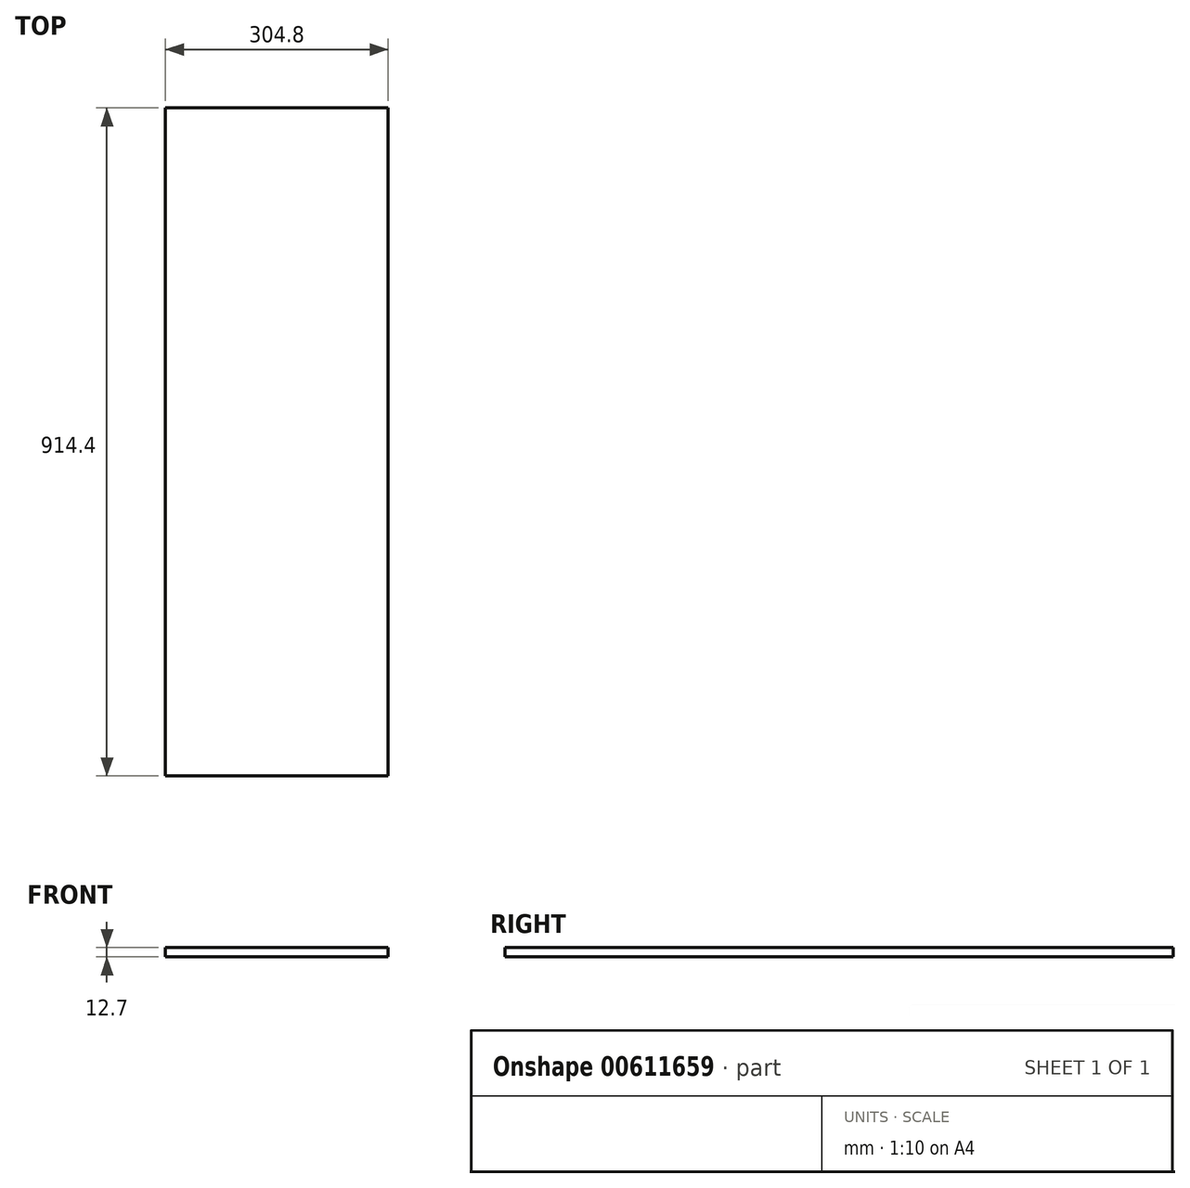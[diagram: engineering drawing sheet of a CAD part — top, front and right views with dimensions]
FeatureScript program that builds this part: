
annotation { "Feature Type Name" : "Feature", "Feature Type Description" : "" }
export const myFeature = defineFeature(function(context is Context, id is Id, definition is map)
    precondition{}
    {
        {
            var Q0;
            Q0=qCreatedBy(makeId("Top.planeOp"),FACE);
            var sketch = newSketch(context, id + "F0", { "sketchPlane" : qUnion([Q0])});
            skLineSegment(sketch, "E0.bottom", {"start": v(-152.4, 457.2) * mm, "end": v(152.4, 457.2) * mm});
            skLineSegment(sketch, "E0.top", {"start": v(-152.4, -457.2) * mm, "end": v(152.4, -457.2) * mm});
            skLineSegment(sketch, "E0.left", {"start": v(-152.4, 457.2) * mm, "end": v(-152.4, -457.2) * mm});
            skLineSegment(sketch, "E0.right", {"start": v(152.4, 457.2) * mm, "end": v(152.4, -457.2) * mm});
            skSolve(sketch);
        }
        {
            var Q0;
            Q0 = qSketchRegion(id + "FfFJr1QY6GmuVDC_0", true);
            var Q1;
            Q1=makeQuery(id+"F0.imprint","IMPRINT",FACE,{"disambiguationData":[TD([[makeQuery(id+"F0.imprint","IMPRINT",EDGE,{"derivedFrom":sQuery(id+"F0.wireOp",EDGE,"E0.bottom")}),-1.0]])]});
            extrude(context, id + "F1", {"entities" : qUnion([Q0, Q1]), "depth" : 12.7 * mm, "offsetDistance" : 25.4 * mm});
        }
    });
